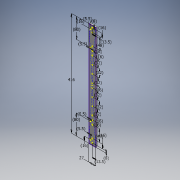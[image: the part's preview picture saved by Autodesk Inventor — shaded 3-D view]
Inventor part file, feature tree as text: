
AUTODESK INVENTOR PART (.ipt)
format: ipt  version: 2016 (Build 200138000, 138)  size: 145,920 bytes
history: native  units: mm
features: reference x21, extrude x1, sketch x1
ambient origin geometry x8: Origin, YZ Plane, XZ Plane, XY Plane, X Axis, Y Axis, Z Axis, Center Point
bodies: Body1 (feature_tree)
feature tree (23):
  extrude  "Extrusion6"  Depth=416.0mm
  sketch  "Sketch1"  dims[d0=27.0mm d1=416.0mm d14=8.0mm d15=5.5mm d16=13.5mm d17=16.0mm d18=80.0mm d19=16.0mm d20=80.0mm d21=16.0mm d22=5.5mm d23=5.5mm d24=8.0mm d25=13.5mm d26=16.0mm d27=16.0mm d28=16.0mm d29=32.0mm d30=32.0mm d31=32.0mm d32=16.0mm d33=32.0mm d34=32.0mm d35=32.0mm d36=16.0mm d37=16.0mm d38=48.0mm d39=48.0mm d40=5.5mm d41=6.0mm d42=0.0mm]
  reference  "Reference1"
  reference  "Reference2"
  reference  "Reference5"
  reference  "Reference6"
  reference  "Reference7"
  reference  "Reference9"
  reference  "Reference11"
  reference  "Reference15"
  reference  "Reference16"
  reference  "Reference17"
  reference  "Reference19"
  reference  "Reference21"
  reference  "Reference23"
  reference  "Reference24"
  reference  "Reference25"
  reference  "Reference28"
  reference  "Reference29"
  reference  "Reference31"
  reference  "Reference32"
  reference  "Reference35"
  reference  "Reference37"
